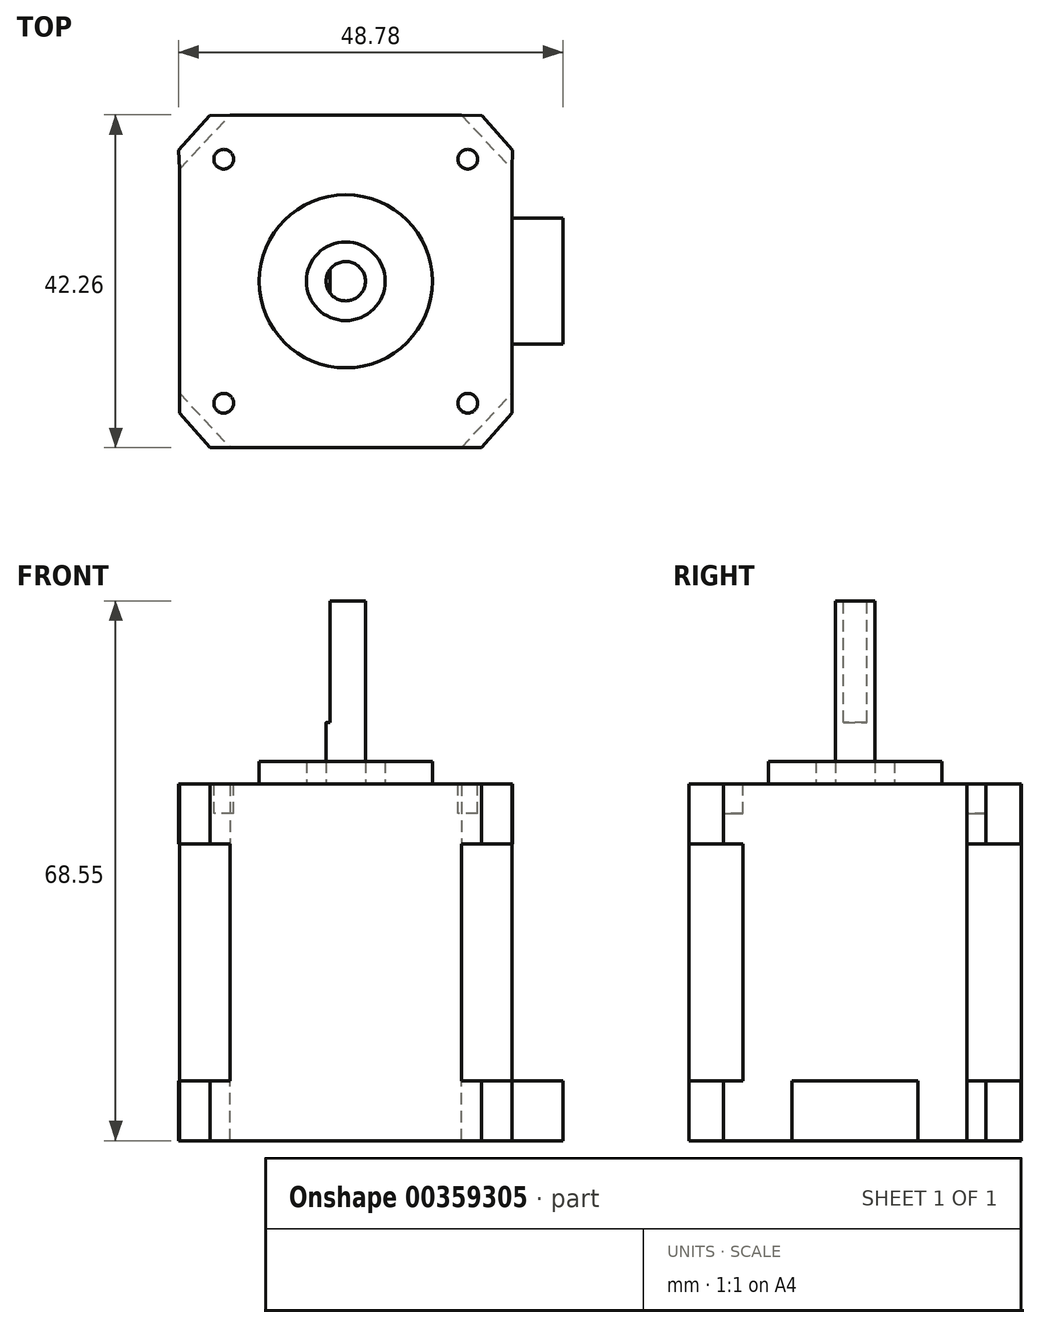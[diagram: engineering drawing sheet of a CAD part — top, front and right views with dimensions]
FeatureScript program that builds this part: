
annotation { "Feature Type Name" : "Feature", "Feature Type Description" : "" }
export const myFeature = defineFeature(function(context is Context, id is Id, definition is map)
    precondition{}
    {
        {
            var Q0;
            Q0=qCreatedBy(makeId("Top.planeOp"),FACE);
            var sketch = newSketch(context, id + "F0", { "sketchPlane" : qUnion([Q0])});
            skLineSegment(sketch, "E0.bottom", {"start": v(14.69, 21.13) * mm, "end": v(-14.69, 21.13) * mm});
            skLineSegment(sketch, "E0.top", {"start": v(14.69, -21.12) * mm, "end": v(-14.69, -21.12) * mm});
            skLineSegment(sketch, "E0.left", {"start": v(21.12, 14.22) * mm, "end": v(21.12, -14.22) * mm});
            skLineSegment(sketch, "E0.right", {"start": v(-21.13, 14.22) * mm, "end": v(-21.13, -14.22) * mm});
            skPoint(sketch, "E0.middle", {"position": v(0, 0) * mm});
            skLineSegment(sketch, "E1", {"start": v(-21.13, -14.22) * mm, "end": v(-14.69, -21.12) * mm});
            skLineSegment(sketch, "E2", {"start": v(14.69, 21.13) * mm, "end": v(21.12, 14.22) * mm});
            skLineSegment(sketch, "E3", {"start": v(-21.13, 14.22) * mm, "end": v(-14.69, 21.13) * mm});
            skLineSegment(sketch, "E4", {"start": v(14.69, -21.12) * mm, "end": v(21.13, -14.22) * mm});
            skSolve(sketch);
        }
        {
            var Q0;
            Q0=makeQuery(id+"F0.imprint","IMPRINT",FACE,{"disambiguationData":[TD([[makeQuery(id+"F0.imprint","IMPRINT",EDGE,{"derivedFrom":sQuery(id+"F0.wireOp",EDGE,"E0.bottom")}),1.0]])]});
            extrude(context, id + "F1", {"entities" : qUnion([Q0]), "depth" : 30.1 * mm, "symmetric" : true});
        }
        {
            var Q0;
            Q0=makeQuery(id+"F1.opExtrude","CAP_FACE",FACE,{"disambiguationData":[OSD([sQuery(id+"F0.wireOp",EDGE,"E0.bottom"),sQuery(id+"F0.wireOp",EDGE,"E0.top"),sQuery(id+"F0.wireOp",EDGE,"E0.left"),sQuery(id+"F0.wireOp",EDGE,"E0.right"),sQuery(id+"F0.wireOp",EDGE,"E1"),sQuery(id+"F0.wireOp",EDGE,"E2"),sQuery(id+"F0.wireOp",EDGE,"E3"),sQuery(id+"F0.wireOp",EDGE,"E4")])],"isStart":false});
            var sketch = newSketch(context, id + "F2", { "sketchPlane" : qUnion([Q0])});
            skLineSegment(sketch, "E5.0", {"start": v(-21.13, 14.22) * mm, "end": v(-21.13, -14.22) * mm});
            skLineSegment(sketch, "E6.2", {"start": v(21.12, 14.22) * mm, "end": v(21.12, -14.22) * mm});
            skLineSegment(sketch, "E6.4", {"start": v(14.69, -21.12) * mm, "end": v(-14.69, -21.12) * mm});
            skLineSegment(sketch, "E7", {"start": v(-21.13, -14.22) * mm, "end": v(-21.13, -16.72) * mm});
            skLineSegment(sketch, "E8", {"start": v(-17.22, -21.12) * mm, "end": v(-14.69, -21.12) * mm});
            skLineSegment(sketch, "E9", {"start": v(14.69, -21.12) * mm, "end": v(17.22, -21.12) * mm});
            skLineSegment(sketch, "E10", {"start": v(21.12, -16.72) * mm, "end": v(21.12, -14.22) * mm});
            skLineSegment(sketch, "E11", {"start": v(21.2, 16.63) * mm, "end": v(21.12, 14.22) * mm});
            skLineSegment(sketch, "E12", {"start": v(-21.2, 16.63) * mm, "end": v(-21.13, 14.22) * mm});
            skLineSegment(sketch, "E13", {"start": v(-21.2, 16.63) * mm, "end": v(-17.3, 21.03) * mm});
            skLineSegment(sketch, "E14", {"start": v(21.2, 16.63) * mm, "end": v(17.3, 21.03) * mm});
            skLineSegment(sketch, "E15", {"start": v(17.22, -21.12) * mm, "end": v(21.12, -16.72) * mm});
            skLineSegment(sketch, "E16", {"start": v(-17.22, -21.12) * mm, "end": v(-21.13, -16.72) * mm});
            skLineSegment(sketch, "E17.0", {"start": v(14.69, 21.13) * mm, "end": v(-14.69, 21.13) * mm});
            skLineSegment(sketch, "E18", {"start": v(14.69, 21.13) * mm, "end": v(17.3, 21.03) * mm});
            skLineSegment(sketch, "E19", {"start": v(-14.69, 21.13) * mm, "end": v(-17.3, 21.03) * mm});
            skSolve(sketch);
        }
        {
            var Q0;
            Q0 = qSketchRegion(id + "F2", true);
            extrude(context, id + "F3", {"entities" : qUnion([Q0]), "depth" : 7.6 * mm});
        }
        {
            var Q0;
            Q0=makeQuery(id+"F3.opExtrude","SWEPT_BODY",BODY,{"disambiguationData":[OSD([sQuery(id+"F2.wireOp",EDGE,"E5.0"),sQuery(id+"F2.wireOp",EDGE,"E6.0"),sQuery(id+"F2.wireOp",EDGE,"E6.2"),sQuery(id+"F2.wireOp",EDGE,"E6.4"),sQuery(id+"F2.wireOp",EDGE,"E7"),sQuery(id+"F2.wireOp",EDGE,"E8"),sQuery(id+"F2.wireOp",EDGE,"E9"),sQuery(id+"F2.wireOp",EDGE,"E10"),sQuery(id+"F2.wireOp",EDGE,"ovVNHEYc-XTPn-S3mz-7e43-ms6itlMq4O8R"),sQuery(id+"F2.wireOp",EDGE,"E11"),sQuery(id+"F2.wireOp",EDGE,"mx7WobmU-6VZ7-vbm9-bB6x-jV2E36fWYEE0"),sQuery(id+"F2.wireOp",EDGE,"E12"),sQuery(id+"F2.wireOp",EDGE,"E13"),sQuery(id+"F2.wireOp",EDGE,"E14"),sQuery(id+"F2.wireOp",EDGE,"E15"),sQuery(id+"F2.wireOp",EDGE,"E16")])]});
            var Q1;
            Q1=qCreatedBy(makeId("Top.planeOp"),FACE);
            mirror(context, id + "F4", {"operationType" : NewBodyOperationType.ADD, "entities" : qUnion([Q0]), "mirrorPlane" : qUnion([Q1])});
        }
        {
            var Q0;
            Q0=makeQuery(id+"F3.opExtrude","CAP_FACE",FACE,{"disambiguationData":[OSD([sQuery(id+"F2.wireOp",EDGE,"E5.0"),sQuery(id+"F2.wireOp",EDGE,"E6.0"),sQuery(id+"F2.wireOp",EDGE,"E6.2"),sQuery(id+"F2.wireOp",EDGE,"E6.4"),sQuery(id+"F2.wireOp",EDGE,"E7"),sQuery(id+"F2.wireOp",EDGE,"E8"),sQuery(id+"F2.wireOp",EDGE,"E9"),sQuery(id+"F2.wireOp",EDGE,"E10"),sQuery(id+"F2.wireOp",EDGE,"ovVNHEYc-XTPn-S3mz-7e43-ms6itlMq4O8R"),sQuery(id+"F2.wireOp",EDGE,"E11"),sQuery(id+"F2.wireOp",EDGE,"mx7WobmU-6VZ7-vbm9-bB6x-jV2E36fWYEE0"),sQuery(id+"F2.wireOp",EDGE,"E12"),sQuery(id+"F2.wireOp",EDGE,"E13"),sQuery(id+"F2.wireOp",EDGE,"E14"),sQuery(id+"F2.wireOp",EDGE,"E15"),sQuery(id+"F2.wireOp",EDGE,"E16")])],"isStart":false});
            var sketch = newSketch(context, id + "F5", { "sketchPlane" : qUnion([Q0])});
            skCircle(sketch, "E20", {"center": v(0, 0) * mm, "radius": 11 * mm});
            skCircle(sketch, "E21", {"center": v(0, 0) * mm, "radius": 2.5 * mm});
            skCircle(sketch, "E22", {"center": v(0, 0) * mm, "radius": 5 * mm});
            skCircle(sketch, "E23.0", {"center": v(15.5, 15.5) * mm, "radius": 1.25 * mm});
            skCircle(sketch, "E24.0", {"center": v(15.5, -15.5) * mm, "radius": 1.25 * mm});
            skCircle(sketch, "E25.0", {"center": v(-15.5, -15.5) * mm, "radius": 1.25 * mm});
            skCircle(sketch, "E26.0", {"center": v(-15.5, 15.5) * mm, "radius": 1.25 * mm});
            skSolve(sketch);
        }
        {
            var Q0;
            Q0=makeQuery(id+"F5.imprint","IMPRINT",FACE,{"disambiguationData":[TD([[makeQuery(id+"F5.imprint","IMPRINT",EDGE,{"derivedFrom":sQuery(id+"F5.wireOp",EDGE,"E20")}),1.0]])]});
            extrude(context, id + "F6", {"entities" : qUnion([Q0]), "operationType" : NewBodyOperationType.ADD, "depth" : 2.9 * mm});
        }
        {
            var Q0;
            Q0=makeQuery(id+"F5.imprint","IMPRINT",FACE,{"disambiguationData":[TD([[makeQuery(id+"F5.imprint","IMPRINT",EDGE,{"derivedFrom":sQuery(id+"F5.wireOp",EDGE,"E21")}),1.0]])]});
            extrude(context, id + "F7", {"entities" : qUnion([Q0]), "operationType" : NewBodyOperationType.ADD, "depth" : 23.25 * mm});
        }
        {
            var Q0;
            Q0=makeQuery(id+"F7.opExtrude","CAP_FACE",FACE,{"disambiguationData":[OSD([sQuery(id+"F5.wireOp",EDGE,"E21")])],"isStart":false});
            var sketch = newSketch(context, id + "F8", { "sketchPlane" : qUnion([Q0])});
            skLineSegment(sketch, "E27", {"start": v(-2, -1.5) * mm, "end": v(-2, 1.5) * mm});
            skSolve(sketch);
        }
        {
            var Q0;
            {var subQ0=sQuery(id+"F8.wireOp",EDGE,"E27");Q0=makeQuery(id+"F8.imprint","IMPRINT",FACE,{"disambiguationData":[TD([[makeQuery(id+"F8.imprint","IMPRINT",EDGE,{"derivedFrom":subQ0}),1.0]])]});}
            extrude(context, id + "F9", {"entities" : qUnion([Q0]), "operationType" : NewBodyOperationType.REMOVE, "oppositeDirection" : true, "depth" : 15.4 * mm});
        }
        {
            var Q0;
            {var subQ0=makeQuery(id+"F3.opExtrude","SWEPT_FACE",FACE,{"disambiguationData":[OSD([sQuery(id+"F2.wireOp",EDGE,"E6.2"),sQuery(id+"F2.wireOp",EDGE,"E10")])]});Q0=makeQuery(id+"F4.boolean.opBoolean","MERGE",FACE,{"derivedFrom":[makeQuery(id+"F1.opExtrude","SWEPT_FACE",FACE,{"disambiguationData":[OSD([sQuery(id+"F0.wireOp",EDGE,"E0.left")])]}),subQ0,makeQuery(id+"F4.opPattern","COPY",FACE,{"derivedFrom":subQ0,"instanceName":"1"})]});}
            var sketch = newSketch(context, id + "F10", { "sketchPlane" : qUnion([Q0])});
            skLineSegment(sketch, "E28.bottom", {"start": v(-8, -22.65) * mm, "end": v(8, -22.65) * mm});
            skLineSegment(sketch, "E28.top", {"start": v(-8, -15.05) * mm, "end": v(8, -15.05) * mm});
            skLineSegment(sketch, "E28.left", {"start": v(-8, -22.65) * mm, "end": v(-8, -15.05) * mm});
            skLineSegment(sketch, "E28.right", {"start": v(8, -22.65) * mm, "end": v(8, -15.05) * mm});
            skPoint(sketch, "E29", {"position": v(0, -15.05) * mm});
            skLineSegment(sketch, "E30.0", {"start": v(16.63, -15.05) * mm, "end": v(21.03, -15.05) * mm});
            skSolve(sketch);
        }
        {
            var Q0;
            Q0 = qSketchRegion(id + "F10", true);
            extrude(context, id + "F11", {"entities" : qUnion([Q0]), "operationType" : NewBodyOperationType.ADD, "depth" : 6.45 * mm});
        }
        {
            var Q0;
            Q0=makeQuery(id+"F5.imprint","IMPRINT",FACE,{"disambiguationData":[TD([[makeQuery(id+"F5.imprint","IMPRINT",EDGE,{"derivedFrom":sQuery(id+"F5.wireOp",EDGE,"E25.0")}),1.0]])]});
            var Q1;
            Q1=makeQuery(id+"F5.imprint","IMPRINT",FACE,{"disambiguationData":[TD([[makeQuery(id+"F5.imprint","IMPRINT",EDGE,{"derivedFrom":sQuery(id+"F5.wireOp",EDGE,"E24.0")}),1.0]])]});
            var Q2;
            Q2=makeQuery(id+"F5.imprint","IMPRINT",FACE,{"disambiguationData":[TD([[makeQuery(id+"F5.imprint","IMPRINT",EDGE,{"derivedFrom":sQuery(id+"F5.wireOp",EDGE,"E23.0")}),1.0]])]});
            var Q3;
            Q3=makeQuery(id+"F5.imprint","IMPRINT",FACE,{"disambiguationData":[TD([[makeQuery(id+"F5.imprint","IMPRINT",EDGE,{"derivedFrom":sQuery(id+"F5.wireOp",EDGE,"E26.0")}),1.0]])]});
            extrude(context, id + "F12", {"entities" : qUnion([Q0, Q1, Q2, Q3]), "operationType" : NewBodyOperationType.REMOVE, "oppositeDirection" : true, "depth" : 3.75 * mm});
        }
    });
